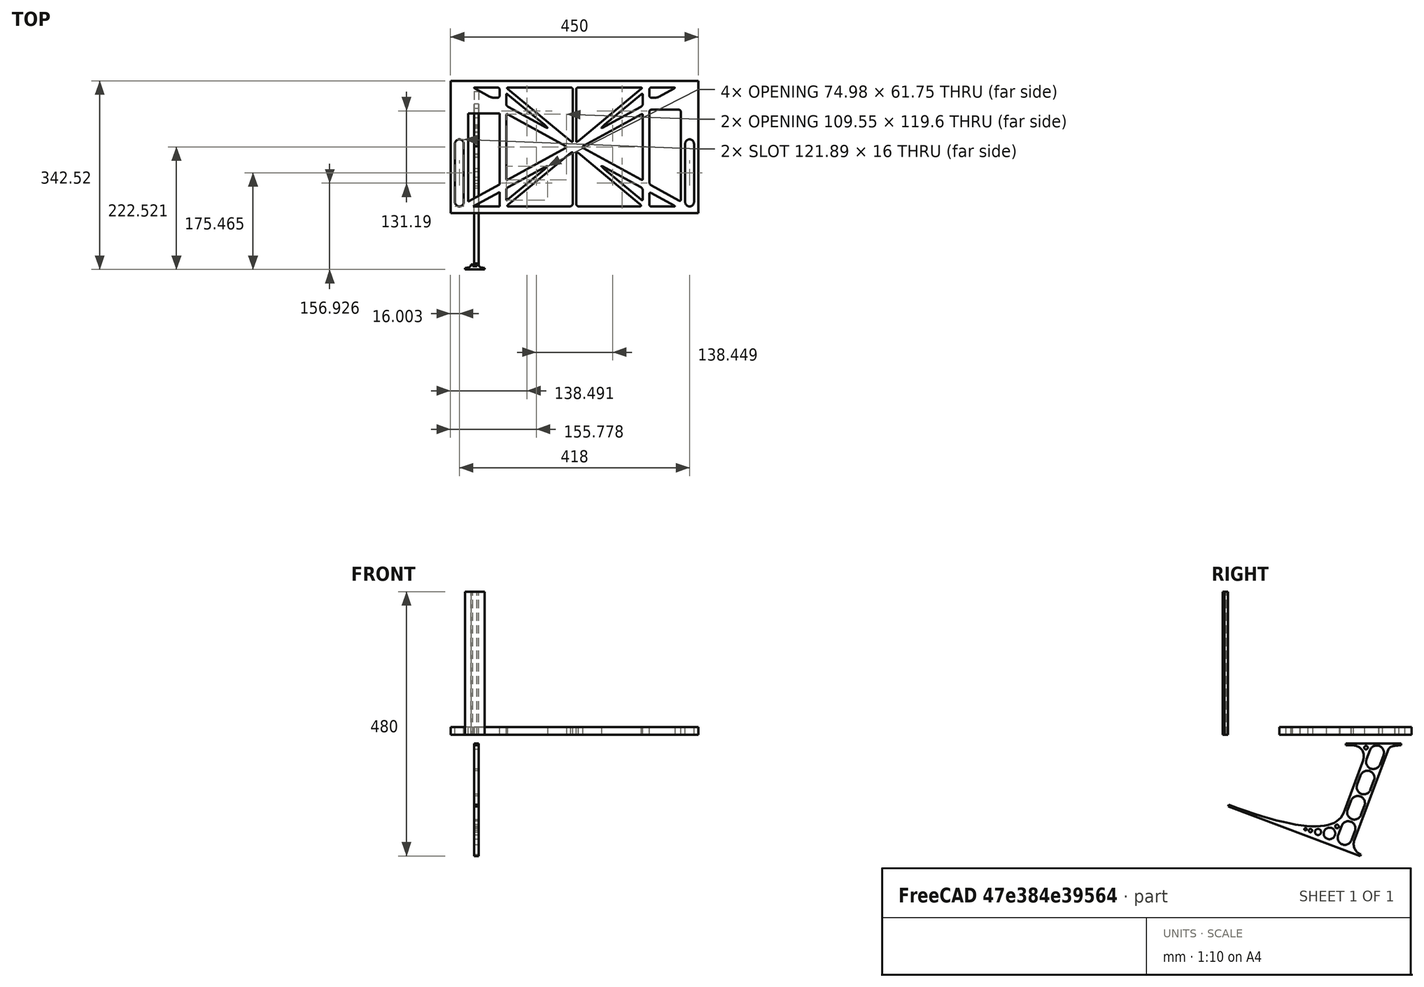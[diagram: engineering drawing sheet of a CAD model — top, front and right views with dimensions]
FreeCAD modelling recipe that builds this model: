
FCSTD DOCUMENT  (FreeCAD 0.19R0.19.2)
Label: laptopStand123FCStd
License: All rights reserved
LicenseURL: http://en.wikipedia.org/wiki/All_rights_reserved
objects: Sketcher::SketchObject×3, Part::Extrusion×3
note: 6 computed .brp shape members not serialized (recipe doc carries the construction recipe); baked Part::Feature solids carry a one-line shape summary decoded from their .brp

FEATURE [Sketcher::SketchObject] Sketch
  FullyConstrained = false
  sketch-geometry (356):
    g0: LineSegment StartX=-10.9272 StartY=-82.7794 StartZ=0 EndX=46.0728 EndY=-51.4823 EndZ=0
    g1: LineSegment StartX=-10.9272 StartY=77.3346 StartZ=0 EndX=-10.9272 EndY=-82.7794 EndZ=0
    g2: LineSegment StartX=46.0728 StartY=-65.424 StartZ=0 EndX=-1.92719 EndY=-91.7794 EndZ=0
    g3: LineSegment StartX=46.0728 StartY=-65.424 StartZ=0 EndX=46.0728 EndY=-91.7794 EndZ=0
    g4: LineSegment StartX=46.0728 StartY=77.3346 StartZ=0 EndX=46.0728 EndY=-51.4823 EndZ=0
    g5: LineSegment StartX=-42.9272 StartY=136.221 StartZ=0 EndX=-42.9272 EndY=-103.779 EndZ=0
    g6: LineSegment StartX=407.073 StartY=136.221 StartZ=0 EndX=407.073 EndY=-103.779 EndZ=0
    g7: ArcOfCircle CenterX=-26.9272 CenterY=22.1087 CenterZ=0 NormalX=0 NormalY=0 NormalZ=1 AngleXU=0 Radius=8 StartAngle=1e-16 EndAngle=3.14159
    g8: ArcOfCircle CenterX=-26.9272 CenterY=-83.7794 CenterZ=0 NormalX=0 NormalY=0 NormalZ=1 AngleXU=0 Radius=8 StartAngle=3.14159 EndAngle=6.28319
    g9: LineSegment StartX=-34.9272 StartY=22.1087 StartZ=0 EndX=-34.9272 EndY=-83.7794 EndZ=0
    g10: LineSegment StartX=-18.9272 StartY=22.1087 StartZ=0 EndX=-18.9272 EndY=-83.7794 EndZ=0
    g11: ArcOfCircle CenterX=391.073 CenterY=22.1087 CenterZ=0 NormalX=0 NormalY=0 NormalZ=1 AngleXU=0 Radius=8 StartAngle=-4.4e-15 EndAngle=3.14159
    g12: LineSegment StartX=399.073 StartY=22.1087 StartZ=0 EndX=399.073 EndY=-83.7794 EndZ=0
    g13: LineSegment StartX=383.073 StartY=22.1087 StartZ=0 EndX=383.073 EndY=-83.7794 EndZ=0
    g14: ArcOfCircle CenterX=391.073 CenterY=-83.7794 CenterZ=0 NormalX=0 NormalY=0 NormalZ=1 AngleXU=0 Radius=8 StartAngle=3.14159 EndAngle=6.28319
    g15: Circle CenterX=175.022 CenterY=27.0628 CenterZ=0 NormalX=0 NormalY=0 NormalZ=1 AngleXU=0 Radius=1
    g16: Circle CenterX=179.022 CenterY=24.8665 CenterZ=0 NormalX=0 NormalY=0 NormalZ=1 AngleXU=0 Radius=1
    g17: Circle CenterX=179.022 CenterY=27.0628 CenterZ=0 NormalX=0 NormalY=0 NormalZ=1 AngleXU=0 Radius=1
    g18: BSplineCurve PolesCount=3 KnotsCount=2 Degree=2 IsPeriodic=0
    g19: GeomPoint X=175.022 Y=27.0628 Z=0
    g20: GeomPoint X=179.022 Y=27.0628 Z=0
    g21: Circle CenterX=189.124 CenterY=27.0628 CenterZ=0 NormalX=0 NormalY=0 NormalZ=1 AngleXU=0 Radius=1
    g22: Circle CenterX=185.124 CenterY=24.8665 CenterZ=0 NormalX=0 NormalY=0 NormalZ=1 AngleXU=0 Radius=1
    g23: Circle CenterX=185.124 CenterY=27.0628 CenterZ=0 NormalX=0 NormalY=0 NormalZ=1 AngleXU=0 Radius=1
    g24: BSplineCurve PolesCount=3 KnotsCount=2 Degree=2 IsPeriodic=0
    g25: GeomPoint X=189.124 Y=27.0628 Z=0
    g26: GeomPoint X=185.124 Y=27.0628 Z=0
    g27: Circle CenterX=175.022 CenterY=5.37834 CenterZ=0 NormalX=0 NormalY=0 NormalZ=1 AngleXU=0 Radius=1
    g28: Circle CenterX=179.022 CenterY=7.57463 CenterZ=0 NormalX=0 NormalY=0 NormalZ=1 AngleXU=0 Radius=1
    g29: Circle CenterX=179.022 CenterY=5.34704 CenterZ=0 NormalX=0 NormalY=0 NormalZ=1 AngleXU=0 Radius=1
    g30: BSplineCurve PolesCount=3 KnotsCount=2 Degree=2 IsPeriodic=0
    g31: GeomPoint X=175.022 Y=5.37834 Z=0
    g32: GeomPoint X=179.022 Y=5.34704 Z=0
    g33: Circle CenterX=189.124 CenterY=5.37834 CenterZ=0 NormalX=0 NormalY=0 NormalZ=1 AngleXU=0 Radius=1
    g34: Circle CenterX=185.124 CenterY=7.57463 CenterZ=0 NormalX=0 NormalY=0 NormalZ=1 AngleXU=0 Radius=1
    g35: Circle CenterX=185.124 CenterY=5.34704 CenterZ=0 NormalX=0 NormalY=0 NormalZ=1 AngleXU=0 Radius=1
    g36: BSplineCurve PolesCount=3 KnotsCount=2 Degree=2 IsPeriodic=0
    g37: GeomPoint X=189.124 Y=5.37834 Z=0
    g38: GeomPoint X=185.124 Y=5.34704 Z=0
    g39: Circle CenterX=165.871 CenterY=18.1458 CenterZ=0 NormalX=0 NormalY=0 NormalZ=1 AngleXU=0 Radius=1
    g40: Circle CenterX=169.377 CenterY=16.2206 CenterZ=0 NormalX=0 NormalY=0 NormalZ=1 AngleXU=0 Radius=1
    g41: Circle CenterX=165.871 CenterY=14.2954 CenterZ=0 NormalX=0 NormalY=0 NormalZ=1 AngleXU=0 Radius=1
    g42: BSplineCurve PolesCount=3 KnotsCount=2 Degree=2 IsPeriodic=0
    g43: GeomPoint X=165.871 Y=18.1458 Z=0
    g44: GeomPoint X=165.871 Y=14.2954 Z=0
    g45: Circle CenterX=198.275 CenterY=18.1458 CenterZ=0 NormalX=0 NormalY=0 NormalZ=1 AngleXU=0 Radius=1
    g46: Circle CenterX=194.768 CenterY=16.2206 CenterZ=0 NormalX=0 NormalY=0 NormalZ=1 AngleXU=0 Radius=1
    g47: Circle CenterX=198.275 CenterY=14.2954 CenterZ=0 NormalX=0 NormalY=0 NormalZ=1 AngleXU=0 Radius=1
    g48: BSplineCurve PolesCount=3 KnotsCount=2 Degree=2 IsPeriodic=0
    g49: GeomPoint X=198.275 Y=18.1458 Z=0
    g50: GeomPoint X=198.275 Y=14.2954 Z=0
    g51: LineSegment StartX=407.073 StartY=-103.779 StartZ=0 EndX=-42.9272 EndY=-103.779 EndZ=0
    g52: LineSegment StartX=407.073 StartY=136.221 StartZ=0 EndX=-42.9272 EndY=136.221 EndZ=0
    g53: LineSegment StartX=46.0728 StartY=77.3346 StartZ=0 EndX=-10.9272 EndY=77.3346 EndZ=0
    g54: Circle CenterX=125.607 CenterY=54.1951 CenterZ=0 NormalX=0 NormalY=0 NormalZ=1 AngleXU=0 Radius=1
    g55: Circle CenterX=139.632 CenterY=46.4944 CenterZ=0 NormalX=0 NormalY=0 NormalZ=1 AngleXU=0 Radius=1
    g56: Circle CenterX=127.326 CenterY=56.7187 CenterZ=0 NormalX=0 NormalY=0 NormalZ=1 AngleXU=0 Radius=1
    g57: BSplineCurve PolesCount=3 KnotsCount=2 Degree=2 IsPeriodic=0
    g58: GeomPoint X=125.607 Y=54.1951 Z=0
    g59: GeomPoint X=127.326 Y=56.7187 Z=0
    g60: Circle CenterX=236.821 CenterY=56.7187 CenterZ=0 NormalX=0 NormalY=0 NormalZ=1 AngleXU=0 Radius=1
    g61: Circle CenterX=224.513 CenterY=46.4944 CenterZ=0 NormalX=0 NormalY=0 NormalZ=1 AngleXU=0 Radius=1
    g62: Circle CenterX=238.538 CenterY=54.1951 CenterZ=0 NormalX=0 NormalY=0 NormalZ=1 AngleXU=0 Radius=1
    g63: BSplineCurve PolesCount=3 KnotsCount=2 Degree=2 IsPeriodic=0
    g64: GeomPoint X=236.821 Y=56.7187 Z=0
    g65: GeomPoint X=238.538 Y=54.1951 Z=0
    g66: Circle CenterX=238.538 CenterY=-21.7539 CenterZ=0 NormalX=0 NormalY=0 NormalZ=1 AngleXU=0 Radius=1
    g67: Circle CenterX=224.513 CenterY=-14.0532 CenterZ=0 NormalX=0 NormalY=0 NormalZ=1 AngleXU=0 Radius=1
    g68: Circle CenterX=236.821 CenterY=-24.2775 CenterZ=0 NormalX=0 NormalY=0 NormalZ=1 AngleXU=0 Radius=1
    g69: BSplineCurve PolesCount=3 KnotsCount=2 Degree=2 IsPeriodic=0
    g70: GeomPoint X=238.538 Y=-21.7539 Z=0
    g71: GeomPoint X=236.821 Y=-24.2775 Z=0
    g72: Circle CenterX=125.607 CenterY=-21.7539 CenterZ=0 NormalX=0 NormalY=0 NormalZ=1 AngleXU=0 Radius=1
    g73: Circle CenterX=139.632 CenterY=-14.0532 CenterZ=0 NormalX=0 NormalY=0 NormalZ=1 AngleXU=0 Radius=1
    g74: Circle CenterX=127.325 CenterY=-24.2775 CenterZ=0 NormalX=0 NormalY=0 NormalZ=1 AngleXU=0 Radius=1
    g75: BSplineCurve PolesCount=3 KnotsCount=2 Degree=2 IsPeriodic=0
    g76: GeomPoint X=125.607 Y=-21.7539 Z=0
    g77: GeomPoint X=127.325 Y=-24.2775 Z=0
    g78: Circle CenterX=302.996 CenterY=111.695 CenterZ=0 NormalX=0 NormalY=0 NormalZ=1 AngleXU=0 Radius=1
    g79: Circle CenterX=306.073 CenterY=114.251 CenterZ=0 NormalX=0 NormalY=0 NormalZ=1 AngleXU=0 Radius=1
    g80: Circle CenterX=306.073 CenterY=110.251 CenterZ=0 NormalX=0 NormalY=0 NormalZ=1 AngleXU=0 Radius=1
    g81: BSplineCurve PolesCount=3 KnotsCount=2 Degree=2 IsPeriodic=0
    g82: GeomPoint X=302.996 Y=111.695 Z=0
    g83: GeomPoint X=306.073 Y=110.251 Z=0
    g84: Circle CenterX=306.073 CenterY=95.2763 CenterZ=0 NormalX=0 NormalY=0 NormalZ=1 AngleXU=0 Radius=1
    g85: Circle CenterX=306.073 CenterY=91.2763 CenterZ=0 NormalX=0 NormalY=0 NormalZ=1 AngleXU=0 Radius=1
    g86: Circle CenterX=302.567 CenterY=89.3511 CenterZ=0 NormalX=0 NormalY=0 NormalZ=1 AngleXU=0 Radius=1
    g87: BSplineCurve PolesCount=3 KnotsCount=2 Degree=2 IsPeriodic=0
    g88: GeomPoint X=306.073 Y=95.2763 Z=0
    g89: GeomPoint X=302.567 Y=89.3511 Z=0
    g90: LineSegment StartX=306.073 StartY=110.251 StartZ=0 EndX=306.073 EndY=95.2763 EndZ=0
    g91: LineSegment StartX=302.996 StartY=111.695 StartZ=0 EndX=236.821 EndY=56.7187 EndZ=0
    g92: LineSegment StartX=238.538 StartY=54.1951 StartZ=0 EndX=302.567 EndY=89.3511 EndZ=0
    g93: Circle CenterX=61.1496 CenterY=111.695 CenterZ=0 NormalX=0 NormalY=0 NormalZ=1 AngleXU=0 Radius=1
    g94: Circle CenterX=58.0728 CenterY=114.251 CenterZ=0 NormalX=0 NormalY=0 NormalZ=1 AngleXU=0 Radius=1
    g95: Circle CenterX=58.0728 CenterY=110.251 CenterZ=0 NormalX=0 NormalY=0 NormalZ=1 AngleXU=0 Radius=1
    g96: BSplineCurve PolesCount=3 KnotsCount=2 Degree=2 IsPeriodic=0
    g97: GeomPoint X=61.1496 Y=111.695 Z=0
    g98: GeomPoint X=58.0728 Y=110.251 Z=0
    g99: Circle CenterX=61.5791 CenterY=89.3511 CenterZ=0 NormalX=0 NormalY=0 NormalZ=1 AngleXU=0 Radius=1
    g100: Circle CenterX=58.0728 CenterY=91.2763 CenterZ=0 NormalX=0 NormalY=0 NormalZ=1 AngleXU=0 Radius=1
    g101: Circle CenterX=58.0728 CenterY=95.2763 CenterZ=0 NormalX=0 NormalY=0 NormalZ=1 AngleXU=0 Radius=1
    g102: BSplineCurve PolesCount=3 KnotsCount=2 Degree=2 IsPeriodic=0
    g103: GeomPoint X=61.5791 Y=89.3511 Z=0
    g104: GeomPoint X=58.0728 Y=95.2763 Z=0
    g105: LineSegment StartX=58.0728 StartY=110.251 StartZ=0 EndX=58.0728 EndY=95.2763 EndZ=0
    g106: LineSegment StartX=61.1496 StartY=111.695 StartZ=0 EndX=127.326 EndY=56.7187 EndZ=0
    g107: LineSegment StartX=125.607 StartY=54.1951 StartZ=0 EndX=61.5791 EndY=89.3511 EndZ=0
    g108: Circle CenterX=61.5791 CenterY=-56.9099 CenterZ=0 NormalX=0 NormalY=0 NormalZ=1 AngleXU=0 Radius=1
    g109: Circle CenterX=58.0728 CenterY=-58.8351 CenterZ=0 NormalX=0 NormalY=0 NormalZ=1 AngleXU=0 Radius=1
    g110: Circle CenterX=58.0728 CenterY=-62.8351 CenterZ=0 NormalX=0 NormalY=0 NormalZ=1 AngleXU=0 Radius=1
    g111: BSplineCurve PolesCount=3 KnotsCount=2 Degree=2 IsPeriodic=0
    g112: GeomPoint X=61.5791 Y=-56.9099 Z=0
    g113: GeomPoint X=58.0728 Y=-62.8351 Z=0
    g114: Circle CenterX=58.0728 CenterY=-77.8102 CenterZ=0 NormalX=0 NormalY=0 NormalZ=1 AngleXU=0 Radius=1
    g115: Circle CenterX=58.0728 CenterY=-81.8102 CenterZ=0 NormalX=0 NormalY=0 NormalZ=1 AngleXU=0 Radius=1
    g116: Circle CenterX=61.1496 CenterY=-79.2541 CenterZ=0 NormalX=0 NormalY=0 NormalZ=1 AngleXU=0 Radius=1
    g117: BSplineCurve PolesCount=3 KnotsCount=2 Degree=2 IsPeriodic=0
    g118: GeomPoint X=58.0728 Y=-77.8102 Z=0
    g119: GeomPoint X=61.1496 Y=-79.2541 Z=0
    g120: LineSegment StartX=58.0728 StartY=-62.8351 StartZ=0 EndX=58.0728 EndY=-77.8102 EndZ=0
    g121: LineSegment StartX=61.1496 StartY=-79.2541 StartZ=0 EndX=127.325 EndY=-24.2775 EndZ=0
    g122: LineSegment StartX=125.607 StartY=-21.7539 StartZ=0 EndX=61.5791 EndY=-56.9099 EndZ=0
    g123: Circle CenterX=302.567 CenterY=-56.9099 CenterZ=0 NormalX=0 NormalY=0 NormalZ=1 AngleXU=0 Radius=1
    g124: Circle CenterX=306.073 CenterY=-58.8351 CenterZ=0 NormalX=0 NormalY=0 NormalZ=1 AngleXU=0 Radius=1
    g125: Circle CenterX=306.073 CenterY=-62.8351 CenterZ=0 NormalX=0 NormalY=0 NormalZ=1 AngleXU=0 Radius=1
    g126: BSplineCurve PolesCount=3 KnotsCount=2 Degree=2 IsPeriodic=0
    g127: GeomPoint X=302.567 Y=-56.9099 Z=0
    g128: GeomPoint X=306.073 Y=-62.8351 Z=0
    g129: Circle CenterX=302.996 CenterY=-79.2541 CenterZ=0 NormalX=0 NormalY=0 NormalZ=1 AngleXU=0 Radius=1
    g130: Circle CenterX=306.073 CenterY=-81.8102 CenterZ=0 NormalX=0 NormalY=0 NormalZ=1 AngleXU=0 Radius=1
    g131: Circle CenterX=306.073 CenterY=-77.8102 CenterZ=0 NormalX=0 NormalY=0 NormalZ=1 AngleXU=0 Radius=1
    g132: BSplineCurve PolesCount=3 KnotsCount=2 Degree=2 IsPeriodic=0
    g133: GeomPoint X=302.996 Y=-79.2541 Z=0
    g134: GeomPoint X=306.073 Y=-77.8102 Z=0
    g135: LineSegment StartX=306.073 StartY=-62.8351 StartZ=0 EndX=306.073 EndY=-77.8102 EndZ=0
    g136: LineSegment StartX=302.996 StartY=-79.2541 StartZ=0 EndX=236.821 EndY=-24.2775 EndZ=0
    g137: LineSegment StartX=238.538 StartY=-21.7539 StartZ=0 EndX=302.567 EndY=-56.9099 EndZ=0
    g138: Circle CenterX=61.6457 CenterY=-88.8112 CenterZ=0 NormalX=0 NormalY=0 NormalZ=1 AngleXU=0 Radius=1
    g139: Circle CenterX=58.0728 CenterY=-91.7794 CenterZ=0 NormalX=0 NormalY=0 NormalZ=1 AngleXU=0 Radius=1
    g140: Circle CenterX=63.9135 CenterY=-91.7794 CenterZ=0 NormalX=0 NormalY=0 NormalZ=1 AngleXU=0 Radius=1
    g141: BSplineCurve PolesCount=3 KnotsCount=2 Degree=2 IsPeriodic=0
    g142: GeomPoint X=61.6457 Y=-88.8112 Z=0
    g143: GeomPoint X=63.9135 Y=-91.7794 Z=0
    g144: Circle CenterX=179.022 CenterY=-85.8163 CenterZ=0 NormalX=0 NormalY=0 NormalZ=1 AngleXU=0 Radius=1
    g145: Circle CenterX=179.022 CenterY=-91.7794 CenterZ=0 NormalX=0 NormalY=0 NormalZ=1 AngleXU=0 Radius=1
    g146: Circle CenterX=171.895 CenterY=-91.7794 CenterZ=0 NormalX=0 NormalY=0 NormalZ=1 AngleXU=0 Radius=1
    g147: BSplineCurve PolesCount=3 KnotsCount=2 Degree=2 IsPeriodic=0
    g148: GeomPoint X=179.022 Y=-85.8163 Z=0
    g149: GeomPoint X=171.895 Y=-91.7794 Z=0
    g150: Circle CenterX=185.124 CenterY=-86.2028 CenterZ=0 NormalX=0 NormalY=0 NormalZ=1 AngleXU=0 Radius=1
    g151: Circle CenterX=185.124 CenterY=-91.7794 CenterZ=0 NormalX=0 NormalY=0 NormalZ=1 AngleXU=0 Radius=1
    g152: Circle CenterX=191.747 CenterY=-91.7794 CenterZ=0 NormalX=0 NormalY=0 NormalZ=1 AngleXU=0 Radius=1
    g153: BSplineCurve PolesCount=3 KnotsCount=2 Degree=2 IsPeriodic=0
    g154: GeomPoint X=185.124 Y=-86.2028 Z=0
    g155: GeomPoint X=191.747 Y=-91.7794 Z=0
    g156: Circle CenterX=299.888 CenterY=-86.6413 CenterZ=0 NormalX=0 NormalY=0 NormalZ=1 AngleXU=0 Radius=1
    g157: Circle CenterX=306.073 CenterY=-91.7794 CenterZ=0 NormalX=0 NormalY=0 NormalZ=1 AngleXU=0 Radius=1
    g158: Circle CenterX=298.776 CenterY=-91.7794 CenterZ=0 NormalX=0 NormalY=0 NormalZ=1 AngleXU=0 Radius=1
    g159: BSplineCurve PolesCount=3 KnotsCount=2 Degree=2 IsPeriodic=0
    g160: GeomPoint X=299.888 Y=-86.6413 Z=0
    g161: GeomPoint X=298.776 Y=-91.7794 Z=0
    g162: LineSegment StartX=189.124 StartY=5.37834 StartZ=0 EndX=299.888 EndY=-86.6413 EndZ=0
    g163: LineSegment StartX=298.776 StartY=-91.7794 StartZ=0 EndX=191.747 EndY=-91.7794 EndZ=0
    g164: LineSegment StartX=185.124 StartY=-86.2028 StartZ=0 EndX=185.124 EndY=5.34704 EndZ=0
    g165: LineSegment StartX=179.022 StartY=5.34704 StartZ=0 EndX=179.022 EndY=-85.8163 EndZ=0
    g166: LineSegment StartX=171.895 StartY=-91.7794 StartZ=0 EndX=63.9135 EndY=-91.7794 EndZ=0
    g167: LineSegment StartX=61.6457 StartY=-88.8112 StartZ=0 EndX=175.022 EndY=5.37834 EndZ=0
    g168: Circle CenterX=302.073 CenterY=124.221 CenterZ=0 NormalX=0 NormalY=0 NormalZ=1 AngleXU=0 Radius=1
    g169: Circle CenterX=306.073 CenterY=124.221 CenterZ=0 NormalX=0 NormalY=0 NormalZ=1 AngleXU=0 Radius=1
    g170: Circle CenterX=302.996 CenterY=121.665 CenterZ=0 NormalX=0 NormalY=0 NormalZ=1 AngleXU=0 Radius=1
    g171: BSplineCurve PolesCount=3 KnotsCount=2 Degree=2 IsPeriodic=0
    g172: GeomPoint X=302.073 Y=124.221 Z=0
    g173: GeomPoint X=302.996 Y=121.665 Z=0
    g174: Circle CenterX=189.124 CenterY=124.221 CenterZ=0 NormalX=0 NormalY=0 NormalZ=1 AngleXU=0 Radius=1
    g175: Circle CenterX=185.124 CenterY=124.221 CenterZ=0 NormalX=0 NormalY=0 NormalZ=1 AngleXU=0 Radius=1
    g176: Circle CenterX=185.124 CenterY=120.221 CenterZ=0 NormalX=0 NormalY=0 NormalZ=1 AngleXU=0 Radius=1
    g177: BSplineCurve PolesCount=3 KnotsCount=2 Degree=2 IsPeriodic=0
    g178: GeomPoint X=189.124 Y=124.221 Z=0
    g179: GeomPoint X=185.124 Y=120.221 Z=0
    g180: Circle CenterX=175.022 CenterY=124.221 CenterZ=0 NormalX=0 NormalY=0 NormalZ=1 AngleXU=0 Radius=1
    g181: Circle CenterX=179.022 CenterY=124.221 CenterZ=0 NormalX=0 NormalY=0 NormalZ=1 AngleXU=0 Radius=1
    g182: Circle CenterX=179.022 CenterY=120.221 CenterZ=0 NormalX=0 NormalY=0 NormalZ=1 AngleXU=0 Radius=1
    g183: BSplineCurve PolesCount=3 KnotsCount=2 Degree=2 IsPeriodic=0
    g184: GeomPoint X=175.022 Y=124.221 Z=0
    g185: GeomPoint X=179.022 Y=120.221 Z=0
    g186: Circle CenterX=62.0728 CenterY=124.221 CenterZ=0 NormalX=0 NormalY=0 NormalZ=1 AngleXU=0 Radius=1
    g187: Circle CenterX=58.0728 CenterY=124.221 CenterZ=0 NormalX=0 NormalY=0 NormalZ=1 AngleXU=0 Radius=1
    g188: Circle CenterX=61.1496 CenterY=121.665 CenterZ=0 NormalX=0 NormalY=0 NormalZ=1 AngleXU=0 Radius=1
    g189: BSplineCurve PolesCount=3 KnotsCount=2 Degree=2 IsPeriodic=0
    g190: GeomPoint X=62.0728 Y=124.221 Z=0
    g191: GeomPoint X=61.1496 Y=121.665 Z=0
    g192: LineSegment StartX=62.0728 StartY=124.221 StartZ=0 EndX=175.022 EndY=124.221 EndZ=0
    g193: LineSegment StartX=179.022 StartY=120.221 StartZ=0 EndX=179.022 EndY=27.0628 EndZ=0
    g194: LineSegment StartX=185.124 StartY=27.0628 StartZ=0 EndX=185.124 EndY=120.221 EndZ=0
    g195: LineSegment StartX=189.124 StartY=124.221 StartZ=0 EndX=302.073 EndY=124.221 EndZ=0
    g196: LineSegment StartX=302.996 StartY=121.665 StartZ=0 EndX=189.124 EndY=27.0628 EndZ=0
    g197: LineSegment StartX=175.022 StartY=27.0628 StartZ=0 EndX=61.1496 EndY=121.665 EndZ=0
    g198: Circle CenterX=61.5791 CenterY=75.4095 CenterZ=0 NormalX=0 NormalY=0 NormalZ=1 AngleXU=0 Radius=1
    g199: Circle CenterX=58.0728 CenterY=77.3346 CenterZ=0 NormalX=0 NormalY=0 NormalZ=1 AngleXU=0 Radius=1
    g200: Circle CenterX=58.0728 CenterY=73.3346 CenterZ=0 NormalX=0 NormalY=0 NormalZ=1 AngleXU=0 Radius=1
    g201: BSplineCurve PolesCount=3 KnotsCount=2 Degree=2 IsPeriodic=0
    g202: GeomPoint X=61.5791 Y=75.4095 Z=0
    g203: GeomPoint X=58.0728 Y=73.3346 Z=0
    g204: Circle CenterX=58.0728 CenterY=-40.8935 CenterZ=0 NormalX=0 NormalY=0 NormalZ=1 AngleXU=0 Radius=1
    g205: Circle CenterX=58.0728 CenterY=-44.8935 CenterZ=0 NormalX=0 NormalY=0 NormalZ=1 AngleXU=0 Radius=1
    g206: Circle CenterX=61.5791 CenterY=-42.9683 CenterZ=0 NormalX=0 NormalY=0 NormalZ=1 AngleXU=0 Radius=1
    g207: BSplineCurve PolesCount=3 KnotsCount=2 Degree=2 IsPeriodic=0
    g208: GeomPoint X=58.0728 Y=-40.8935 Z=0
    g209: GeomPoint X=61.5791 Y=-42.9683 Z=0
    g210: LineSegment StartX=61.5791 StartY=-42.9683 StartZ=0 EndX=165.871 EndY=14.2954 EndZ=0
    g211: LineSegment StartX=165.871 StartY=18.1458 StartZ=0 EndX=61.5791 EndY=75.4095 EndZ=0
    g212: LineSegment StartX=58.0728 StartY=73.3346 StartZ=0 EndX=58.0728 EndY=-40.8935 EndZ=0
    g213: Circle CenterX=302.567 CenterY=-42.9683 CenterZ=0 NormalX=0 NormalY=0 NormalZ=1 AngleXU=0 Radius=1
    g214: Circle CenterX=306.073 CenterY=-44.8935 CenterZ=0 NormalX=0 NormalY=0 NormalZ=1 AngleXU=0 Radius=1
    g215: Circle CenterX=306.073 CenterY=-40.8935 CenterZ=0 NormalX=0 NormalY=0 NormalZ=1 AngleXU=0 Radius=1
    g216: BSplineCurve PolesCount=3 KnotsCount=2 Degree=2 IsPeriodic=0
    g217: GeomPoint X=302.567 Y=-42.9683 Z=0
    g218: GeomPoint X=306.073 Y=-40.8935 Z=0
    g219: Circle CenterX=306.073 CenterY=73.3346 CenterZ=0 NormalX=0 NormalY=0 NormalZ=1 AngleXU=0 Radius=1
    g220: Circle CenterX=306.073 CenterY=77.3346 CenterZ=0 NormalX=0 NormalY=0 NormalZ=1 AngleXU=0 Radius=1
    g221: Circle CenterX=302.567 CenterY=75.4095 CenterZ=0 NormalX=0 NormalY=0 NormalZ=1 AngleXU=0 Radius=1
    g222: BSplineCurve PolesCount=3 KnotsCount=2 Degree=2 IsPeriodic=0
    g223: GeomPoint X=306.073 Y=73.3346 Z=0
    g224: GeomPoint X=302.567 Y=75.4095 Z=0
    g225: LineSegment StartX=302.567 StartY=-42.9683 StartZ=0 EndX=198.275 EndY=14.2954 EndZ=0
    g226: LineSegment StartX=198.275 StartY=18.1458 StartZ=0 EndX=302.567 EndY=75.4095 EndZ=0
    g227: LineSegment StartX=306.073 StartY=73.3346 StartZ=0 EndX=306.073 EndY=-40.8935 EndZ=0
    g228: LineSegment StartX=322.073 StartY=105.865 StartZ=0 EndX=328.643 EndY=105.865 EndZ=0
    g229: LineSegment StartX=318.073 StartY=120.221 StartZ=0 EndX=318.073 EndY=109.865 EndZ=0
    g230: LineSegment StartX=336.157 StartY=107.779 StartZ=0 EndX=362.567 EndY=122.294 EndZ=0
    g231: Circle CenterX=362.073 CenterY=124.221 CenterZ=0 NormalX=0 NormalY=0 NormalZ=1 AngleXU=0 Radius=1
    g232: Circle CenterX=366.073 CenterY=124.221 CenterZ=0 NormalX=0 NormalY=0 NormalZ=1 AngleXU=0 Radius=1
    g233: Circle CenterX=362.567 CenterY=122.294 CenterZ=0 NormalX=0 NormalY=0 NormalZ=1 AngleXU=0 Radius=1
    g234: BSplineCurve PolesCount=3 KnotsCount=2 Degree=2 IsPeriodic=0
    g235: GeomPoint X=362.073 Y=124.221 Z=0
    g236: GeomPoint X=362.567 Y=122.294 Z=0
    g237: Circle CenterX=322.073 CenterY=124.221 CenterZ=0 NormalX=0 NormalY=0 NormalZ=1 AngleXU=0 Radius=1
    g238: Circle CenterX=318.073 CenterY=124.221 CenterZ=0 NormalX=0 NormalY=0 NormalZ=1 AngleXU=0 Radius=1
    g239: Circle CenterX=318.073 CenterY=120.221 CenterZ=0 NormalX=0 NormalY=0 NormalZ=1 AngleXU=0 Radius=1
    g240: BSplineCurve PolesCount=3 KnotsCount=2 Degree=2 IsPeriodic=0
    g241: GeomPoint X=322.073 Y=124.221 Z=0
    g242: GeomPoint X=318.073 Y=120.221 Z=0
    g243: Circle CenterX=322.073 CenterY=105.865 CenterZ=0 NormalX=0 NormalY=0 NormalZ=1 AngleXU=0 Radius=1
    g244: Circle CenterX=318.073 CenterY=105.865 CenterZ=0 NormalX=0 NormalY=0 NormalZ=1 AngleXU=0 Radius=1
    g245: Circle CenterX=318.073 CenterY=109.865 CenterZ=0 NormalX=0 NormalY=0 NormalZ=1 AngleXU=0 Radius=1
    g246: BSplineCurve PolesCount=3 KnotsCount=2 Degree=2 IsPeriodic=0
    g247: GeomPoint X=322.073 Y=105.865 Z=0
    g248: GeomPoint X=318.073 Y=109.865 Z=0
    g249: Circle CenterX=336.157 CenterY=107.779 CenterZ=0 NormalX=0 NormalY=0 NormalZ=1 AngleXU=0 Radius=1
    g250: Circle CenterX=332.651 CenterY=105.853 CenterZ=0 NormalX=0 NormalY=0 NormalZ=1 AngleXU=0 Radius=1
    g251: Circle CenterX=328.643 CenterY=105.865 CenterZ=0 NormalX=0 NormalY=0 NormalZ=1 AngleXU=0 Radius=1
    g252: BSplineCurve PolesCount=3 KnotsCount=2 Degree=2 IsPeriodic=0
    g253: GeomPoint X=336.157 Y=107.779 Z=0
    g254: GeomPoint X=328.643 Y=105.865 Z=0
    g255: LineSegment StartX=322.073 StartY=124.221 StartZ=0 EndX=362.073 EndY=124.221 EndZ=0
    g256: Circle CenterX=371.567 CenterY=-80.8644 CenterZ=0 NormalX=0 NormalY=0 NormalZ=1 AngleXU=0 Radius=1
    g257: Circle CenterX=375.073 CenterY=-82.7896 CenterZ=0 NormalX=0 NormalY=0 NormalZ=1 AngleXU=0 Radius=1
    g258: Circle CenterX=375.073 CenterY=-78.7896 CenterZ=0 NormalX=0 NormalY=0 NormalZ=1 AngleXU=0 Radius=1
    g259: BSplineCurve PolesCount=3 KnotsCount=2 Degree=2 IsPeriodic=0
    g260: GeomPoint X=371.567 Y=-80.8644 Z=0
    g261: GeomPoint X=375.073 Y=-78.7896 Z=0
    g262: Circle CenterX=321.579 CenterY=-53.4075 CenterZ=0 NormalX=0 NormalY=0 NormalZ=1 AngleXU=0 Radius=1
    g263: Circle CenterX=318.073 CenterY=-51.4823 CenterZ=0 NormalX=0 NormalY=0 NormalZ=1 AngleXU=0 Radius=1
    g264: Circle CenterX=318.073 CenterY=-47.4823 CenterZ=0 NormalX=0 NormalY=0 NormalZ=1 AngleXU=0 Radius=1
    g265: BSplineCurve PolesCount=3 KnotsCount=2 Degree=2 IsPeriodic=0
    g266: GeomPoint X=321.579 Y=-53.4075 Z=0
    g267: GeomPoint X=318.073 Y=-47.4823 Z=0
    g268: Circle CenterX=318.073 CenterY=79.9235 CenterZ=0 NormalX=0 NormalY=0 NormalZ=1 AngleXU=0 Radius=1
    g269: Circle CenterX=318.073 CenterY=83.9235 CenterZ=0 NormalX=0 NormalY=0 NormalZ=1 AngleXU=0 Radius=1
    g270: Circle CenterX=322.073 CenterY=83.9235 CenterZ=0 NormalX=0 NormalY=0 NormalZ=1 AngleXU=0 Radius=1
    g271: BSplineCurve PolesCount=3 KnotsCount=2 Degree=2 IsPeriodic=0
    g272: GeomPoint X=318.073 Y=79.9235 Z=0
    g273: GeomPoint X=322.073 Y=83.9235 Z=0
    g274: Circle CenterX=375.073 CenterY=79.9235 CenterZ=0 NormalX=0 NormalY=0 NormalZ=1 AngleXU=0 Radius=1
    g275: Circle CenterX=375.073 CenterY=83.9235 CenterZ=0 NormalX=0 NormalY=0 NormalZ=1 AngleXU=0 Radius=1
    g276: Circle CenterX=371.073 CenterY=83.9235 CenterZ=0 NormalX=0 NormalY=0 NormalZ=1 AngleXU=0 Radius=1
    g277: BSplineCurve PolesCount=3 KnotsCount=2 Degree=2 IsPeriodic=0
    g278: GeomPoint X=375.073 Y=79.9235 Z=0
    g279: GeomPoint X=371.073 Y=83.9235 Z=0
    g280: LineSegment StartX=322.073 StartY=83.9235 StartZ=0 EndX=371.073 EndY=83.9235 EndZ=0
    g281: LineSegment StartX=375.073 StartY=79.9235 StartZ=0 EndX=375.073 EndY=-78.7896 EndZ=0
    g282: LineSegment StartX=371.567 StartY=-80.8644 StartZ=0 EndX=321.579 EndY=-53.4075 EndZ=0
    g283: LineSegment StartX=318.073 StartY=-47.4823 StartZ=0 EndX=318.073 EndY=79.9235 EndZ=0
    g284: Circle CenterX=321.579 CenterY=-67.3492 CenterZ=0 NormalX=0 NormalY=0 NormalZ=1 AngleXU=0 Radius=1
    g285: Circle CenterX=318.073 CenterY=-65.424 CenterZ=0 NormalX=0 NormalY=0 NormalZ=1 AngleXU=0 Radius=1
    g286: Circle CenterX=318.073 CenterY=-69.424 CenterZ=0 NormalX=0 NormalY=0 NormalZ=1 AngleXU=0 Radius=1
    g287: BSplineCurve PolesCount=3 KnotsCount=2 Degree=2 IsPeriodic=0
    g288: GeomPoint X=321.579 Y=-67.3492 Z=0
    g289: GeomPoint X=318.073 Y=-69.424 Z=0
    g290: Circle CenterX=362.567 CenterY=-89.8542 CenterZ=0 NormalX=0 NormalY=0 NormalZ=1 AngleXU=0 Radius=1
    g291: Circle CenterX=366.073 CenterY=-91.7794 CenterZ=0 NormalX=0 NormalY=0 NormalZ=1 AngleXU=0 Radius=1
    g292: Circle CenterX=362.073 CenterY=-91.7794 CenterZ=0 NormalX=0 NormalY=0 NormalZ=1 AngleXU=0 Radius=1
    g293: BSplineCurve PolesCount=3 KnotsCount=2 Degree=2 IsPeriodic=0
    g294: GeomPoint X=362.567 Y=-89.8542 Z=0
    g295: GeomPoint X=362.073 Y=-91.7794 Z=0
    g296: Circle CenterX=322.073 CenterY=-91.7794 CenterZ=0 NormalX=0 NormalY=0 NormalZ=1 AngleXU=0 Radius=1
    g297: Circle CenterX=318.073 CenterY=-91.7794 CenterZ=0 NormalX=0 NormalY=0 NormalZ=1 AngleXU=0 Radius=1
    g298: Circle CenterX=318.073 CenterY=-87.7794 CenterZ=0 NormalX=0 NormalY=0 NormalZ=1 AngleXU=0 Radius=1
    g299: BSplineCurve PolesCount=3 KnotsCount=2 Degree=2 IsPeriodic=0
    g300: GeomPoint X=322.073 Y=-91.7794 Z=0
    g301: GeomPoint X=318.073 Y=-87.7794 Z=0
    g302: LineSegment StartX=362.567 StartY=-89.8542 StartZ=0 EndX=321.579 EndY=-67.3492 EndZ=0
    g303: LineSegment StartX=318.073 StartY=-69.424 StartZ=0 EndX=318.073 EndY=-87.7794 EndZ=0
    g304: LineSegment StartX=322.073 StartY=-91.7794 StartZ=0 EndX=362.073 EndY=-91.7794 EndZ=0
    g305: Circle CenterX=2.07281 CenterY=124.221 CenterZ=0 NormalX=0 NormalY=0 NormalZ=1 AngleXU=0 Radius=1
    g306: Circle CenterX=1.57905 CenterY=122.295 CenterZ=0 NormalX=0 NormalY=0 NormalZ=1 AngleXU=0 Radius=1
    g307: BSplineCurve PolesCount=3 KnotsCount=2 Degree=2 IsPeriodic=0
    g308: GeomPoint X=2.07281 Y=124.221 Z=0
    g309: GeomPoint X=1.57905 Y=122.295 Z=0
    g310: Circle CenterX=42.0728 CenterY=124.221 CenterZ=0 NormalX=0 NormalY=0 NormalZ=1 AngleXU=0 Radius=1
    g311: Circle CenterX=46.0728 CenterY=124.221 CenterZ=0 NormalX=0 NormalY=0 NormalZ=1 AngleXU=0 Radius=1
    g312: Circle CenterX=46.0728 CenterY=120.221 CenterZ=0 NormalX=0 NormalY=0 NormalZ=1 AngleXU=0 Radius=1
    g313: BSplineCurve PolesCount=3 KnotsCount=2 Degree=2 IsPeriodic=0
    g314: GeomPoint X=42.0728 Y=124.221 Z=0
    g315: GeomPoint X=46.0728 Y=120.221 Z=0
    g316: Circle CenterX=46.0728 CenterY=109.865 CenterZ=0 NormalX=0 NormalY=0 NormalZ=1 AngleXU=0 Radius=1
    g317: Circle CenterX=46.0728 CenterY=105.865 CenterZ=0 NormalX=0 NormalY=0 NormalZ=1 AngleXU=0 Radius=1
    g318: Circle CenterX=42.0728 CenterY=105.865 CenterZ=0 NormalX=0 NormalY=0 NormalZ=1 AngleXU=0 Radius=1
    g319: BSplineCurve PolesCount=3 KnotsCount=2 Degree=2 IsPeriodic=0
    g320: GeomPoint X=46.0728 Y=109.865 Z=0
    g321: GeomPoint X=42.0728 Y=105.865 Z=0
    g322: Circle CenterX=35.5028 CenterY=105.865 CenterZ=0 NormalX=0 NormalY=0 NormalZ=1 AngleXU=0 Radius=1
    g323: Circle CenterX=31.5028 CenterY=105.865 CenterZ=0 NormalX=0 NormalY=0 NormalZ=1 AngleXU=0 Radius=1
    g324: Circle CenterX=27.9965 CenterY=107.79 CenterZ=0 NormalX=0 NormalY=0 NormalZ=1 AngleXU=0 Radius=1
    g325: BSplineCurve PolesCount=3 KnotsCount=2 Degree=2 IsPeriodic=0
    g326: GeomPoint X=35.5028 Y=105.865 Z=0
    g327: GeomPoint X=27.9965 Y=107.79 Z=0
    g328: LineSegment StartX=2.07281 StartY=124.221 StartZ=0 EndX=42.0728 EndY=124.221 EndZ=0
    g329: LineSegment StartX=46.0728 StartY=120.221 StartZ=0 EndX=46.0728 EndY=109.865 EndZ=0
    g330: LineSegment StartX=42.0728 StartY=105.865 StartZ=0 EndX=35.5028 EndY=105.865 EndZ=0
    g331: LineSegment StartX=27.9965 StartY=107.79 StartZ=0 EndX=1.57905 EndY=122.295 EndZ=0
    g332: LineSegment StartX=46.0728 StartY=-65.424 StartZ=0 EndX=46.0728 EndY=-69.424 EndZ=0
    g333: LineSegment StartX=46.0728 StartY=-91.7794 StartZ=0 EndX=46.0728 EndY=-87.7794 EndZ=0
    g334: LineSegment StartX=46.0728 StartY=-91.7794 StartZ=0 EndX=42.0728 EndY=-91.7794 EndZ=0
    g335: LineSegment StartX=-1.92719 StartY=-91.7794 StartZ=0 EndX=2.07281 EndY=-91.7794 EndZ=0
    g336: LineSegment StartX=-1.92719 StartY=-91.7794 StartZ=0 EndX=1.57905 EndY=-89.8542 EndZ=0
    g337: LineSegment StartX=46.0728 StartY=-65.424 StartZ=0 EndX=42.5666 EndY=-67.3492 EndZ=0
    g338: Circle CenterX=42.5666 CenterY=-67.3492 CenterZ=0 NormalX=0 NormalY=0 NormalZ=1 AngleXU=0 Radius=1
    g339: Circle CenterX=46.0728 CenterY=-65.424 CenterZ=0 NormalX=0 NormalY=0 NormalZ=1 AngleXU=0 Radius=1
    g340: Circle CenterX=46.0728 CenterY=-69.424 CenterZ=0 NormalX=0 NormalY=0 NormalZ=1 AngleXU=0 Radius=1
    g341: BSplineCurve PolesCount=3 KnotsCount=2 Degree=2 IsPeriodic=0
    g342: GeomPoint X=42.5666 Y=-67.3492 Z=0
    g343: GeomPoint X=46.0728 Y=-69.424 Z=0
    g344: Circle CenterX=46.0728 CenterY=-87.7794 CenterZ=0 NormalX=0 NormalY=0 NormalZ=1 AngleXU=0 Radius=1
    g345: Circle CenterX=46.0728 CenterY=-91.7794 CenterZ=0 NormalX=0 NormalY=0 NormalZ=1 AngleXU=0 Radius=1
    g346: Circle CenterX=42.0728 CenterY=-91.7794 CenterZ=0 NormalX=0 NormalY=0 NormalZ=1 AngleXU=0 Radius=1
    g347: BSplineCurve PolesCount=3 KnotsCount=2 Degree=2 IsPeriodic=0
    g348: GeomPoint X=46.0728 Y=-87.7794 Z=0
    g349: GeomPoint X=42.0728 Y=-91.7794 Z=0
    g350: Circle CenterX=2.07281 CenterY=-91.7794 CenterZ=0 NormalX=0 NormalY=0 NormalZ=1 AngleXU=0 Radius=1
    g351: Circle CenterX=-1.92719 CenterY=-91.7794 CenterZ=0 NormalX=0 NormalY=0 NormalZ=1 AngleXU=0 Radius=1
    g352: Circle CenterX=1.57905 CenterY=-89.8542 CenterZ=0 NormalX=0 NormalY=0 NormalZ=1 AngleXU=0 Radius=1
    g353: BSplineCurve PolesCount=3 KnotsCount=2 Degree=2 IsPeriodic=0
    g354: GeomPoint X=2.07281 Y=-91.7794 Z=0
    g355: GeomPoint X=1.57905 Y=-89.8542 Z=0
  constraints (600):
    c: Coincident(g3,g2)
    c: Coincident(g0,g4)
    c: Block(g3)
    c: Block(g2)
    c: Block(g0)
    c: Block(g1)
    c: Vertical(g5)
    c: Vertical(g6)
    c: Block(g6)
    c: Block(g5)
    c: Tangent(g7,g10) = 1.5708
    c: Tangent(g7,g9) = -1.5708
    c: Tangent(g9,g8) = -1.5708
    c: Tangent(g10,g8) = 1.5708
    c: Vertical(g9)
    c: Equal(g7,g8)
    c: Block(g10)
    c: Block(g9)
    c: Tangent(g11,g12) = 1.5708
    c: Tangent(g12,g14) = 1.5708
    c: Equal(g11,g14)
    c: Coincident(g13,g11)
    c: Coincident(g13,g14)
    c: Block(g12)
    c: Block(g13)
    c: Weight(g15) = 1
    c: Equal(g15,g16)
    c: Equal(g15,g17)
    c: InternalAlignment(g15,g18)
    c: InternalAlignment(g16,g18)
    c: InternalAlignment(g17,g18)
    c: InternalAlignment(g19,g18)
    c: InternalAlignment(g20,g18)
    c: Weight(g21) = 1
    c: Equal(g21,g22)
    c: Equal(g21,g23)
    c: InternalAlignment(g21,g24)
    c: InternalAlignment(g22,g24)
    c: InternalAlignment(g23,g24)
    c: InternalAlignment(g25,g24)
    c: InternalAlignment(g26,g24)
    c: Block(g24)
    c: Block(g18)
    c: Weight(g27) = 1
    c: Equal(g27,g28)
    c: Equal(g27,g29)
    c: InternalAlignment(g27,g30)
    c: InternalAlignment(g28,g30)
    c: InternalAlignment(g29,g30)
    c: InternalAlignment(g31,g30)
    c: InternalAlignment(g32,g30)
    c: Weight(g33) = 1
    c: Equal(g33,g34)
    c: Equal(g33,g35)
    c: InternalAlignment(g33,g36)
    c: InternalAlignment(g34,g36)
    c: InternalAlignment(g35,g36)
    c: InternalAlignment(g37,g36)
    c: InternalAlignment(g38,g36)
    c: Block(g36)
    c: Block(g30)
    c: Weight(g39) = 1
    c: Equal(g39,g40)
    c: Equal(g39,g41)
    c: InternalAlignment(g39,g42)
    c: InternalAlignment(g40,g42)
    c: InternalAlignment(g41,g42)
    c: InternalAlignment(g43,g42)
    c: InternalAlignment(g44,g42)
    c: Weight(g45) = 1
    c: Equal(g45,g46)
    c: Equal(g45,g47)
    c: InternalAlignment(g45,g48)
    c: InternalAlignment(g46,g48)
    c: InternalAlignment(g47,g48)
    c: InternalAlignment(g49,g48)
    c: InternalAlignment(g50,g48)
    c: Block(g42)
    c: Block(g48)
    c: Coincident(g51,g6)
    c: Coincident(g51,g5)
    c: Horizontal(g51)
    c: Distance(g51) = 450
    c: Coincident(g52,g6)
    c: Coincident(g52,g5)
    c: Horizontal(g52)
    c: Horizontal(g53)
    c: Coincident(g4,g53)
    c: Block(g53)
    c: Coincident(g1,g53)
    c: Weight(g54) = 1
    c: Equal(g54,g55)
    c: Equal(g54,g56)
    c: InternalAlignment(g54,g57)
    c: InternalAlignment(g55,g57)
    c: InternalAlignment(g56,g57)
    c: InternalAlignment(g58,g57)
    c: InternalAlignment(g59,g57)
    c: Block(g57)
    c: Weight(g60) = 1
    c: Equal(g60,g61)
    c: Equal(g60,g62)
    c: InternalAlignment(g60,g63)
    c: InternalAlignment(g61,g63)
    c: InternalAlignment(g62,g63)
    c: InternalAlignment(g64,g63)
    c: InternalAlignment(g65,g63)
    c: Block(g63)
    c: Weight(g66) = 1
    c: Equal(g66,g67)
    c: Equal(g66,g68)
    c: InternalAlignment(g66,g69)
    c: InternalAlignment(g67,g69)
    c: InternalAlignment(g68,g69)
    c: InternalAlignment(g70,g69)
    c: InternalAlignment(g71,g69)
    c: Block(g69)
    c: Weight(g72) = 1
    c: Equal(g72,g73)
    c: Equal(g72,g74)
    c: InternalAlignment(g72,g75)
    c: InternalAlignment(g73,g75)
    c: InternalAlignment(g74,g75)
    c: InternalAlignment(g76,g75)
    c: InternalAlignment(g77,g75)
    c: Block(g75)
    c: Weight(g78) = 1
    c: Equal(g78,g79)
    c: Equal(g78,g80)
    c: InternalAlignment(g78,g81)
    c: InternalAlignment(g79,g81)
    c: InternalAlignment(g80,g81)
    c: InternalAlignment(g82,g81)
    c: InternalAlignment(g83,g81)
    c: Weight(g84) = 1
    c: Equal(g84,g85)
    c: Equal(g84,g86)
    c: InternalAlignment(g84,g87)
    c: InternalAlignment(g85,g87)
    c: InternalAlignment(g86,g87)
    c: InternalAlignment(g88,g87)
    c: InternalAlignment(g89,g87)
    c: Block(g81)
    c: Block(g87)
    c: Coincident(g90,g81)
    c: Coincident(g90,g87)
    c: Vertical(g90)
    c: Coincident(g91,g81)
    c: Coincident(g91,g63)
    c: Coincident(g92,g63)
    c: Coincident(g92,g87)
    c: Weight(g93) = 1
    c: Equal(g93,g94)
    c: Equal(g93,g95)
    c: InternalAlignment(g93,g96)
    c: InternalAlignment(g94,g96)
    c: InternalAlignment(g95,g96)
    c: InternalAlignment(g97,g96)
    c: InternalAlignment(g98,g96)
    c: Weight(g99) = 1
    c: Equal(g99,g100)
    c: Equal(g99,g101)
    c: InternalAlignment(g99,g102)
    c: InternalAlignment(g100,g102)
    c: InternalAlignment(g101,g102)
    c: InternalAlignment(g103,g102)
    c: InternalAlignment(g104,g102)
    c: Block(g96)
    c: Block(g102)
    c: Coincident(g105,g96)
    c: Coincident(g105,g102)
    c: Vertical(g105)
    c: Coincident(g106,g96)
    c: Coincident(g106,g57)
    c: Coincident(g107,g57)
    c: Coincident(g107,g102)
    c: Weight(g108) = 1
    c: Equal(g108,g109)
    c: Equal(g108,g110)
    c: InternalAlignment(g108,g111)
    c: InternalAlignment(g109,g111)
    c: InternalAlignment(g110,g111)
    c: InternalAlignment(g112,g111)
    c: InternalAlignment(g113,g111)
    c: Weight(g114) = 1
    c: Equal(g114,g115)
    c: Equal(g114,g116)
    c: InternalAlignment(g114,g117)
    c: InternalAlignment(g115,g117)
    c: InternalAlignment(g116,g117)
    c: InternalAlignment(g118,g117)
    c: InternalAlignment(g119,g117)
    c: Block(g111)
    c: Block(g117)
    c: Coincident(g120,g111)
    c: Coincident(g120,g117)
    c: Vertical(g120)
    c: Coincident(g121,g117)
    c: Coincident(g121,g75)
    c: Coincident(g122,g75)
    c: Coincident(g122,g111)
    c: Weight(g123) = 1
    c: Equal(g123,g124)
    c: Equal(g123,g125)
    c: InternalAlignment(g123,g126)
    c: InternalAlignment(g124,g126)
    c: InternalAlignment(g125,g126)
    c: InternalAlignment(g127,g126)
    c: InternalAlignment(g128,g126)
    c: Weight(g129) = 1
    c: Equal(g129,g130)
    c: Equal(g129,g131)
    c: InternalAlignment(g129,g132)
    c: InternalAlignment(g130,g132)
    c: InternalAlignment(g131,g132)
    c: InternalAlignment(g133,g132)
    c: InternalAlignment(g134,g132)
    c: Block(g126)
    c: Block(g132)
    c: Coincident(g135,g126)
    c: Coincident(g135,g132)
    c: Vertical(g135)
    c: Coincident(g136,g132)
    c: Coincident(g136,g69)
    c: Coincident(g137,g69)
    c: Coincident(g137,g126)
    c: Weight(g138) = 1
    c: Equal(g138,g139)
    c: Equal(g138,g140)
    c: InternalAlignment(g138,g141)
    c: InternalAlignment(g139,g141)
    c: InternalAlignment(g140,g141)
    c: InternalAlignment(g142,g141)
    c: InternalAlignment(g143,g141)
    c: Weight(g144) = 1
    c: Equal(g144,g145)
    c: Equal(g144,g146)
    c: InternalAlignment(g144,g147)
    c: InternalAlignment(g145,g147)
    c: InternalAlignment(g146,g147)
    c: InternalAlignment(g148,g147)
    c: InternalAlignment(g149,g147)
    c: Weight(g150) = 1
    c: Equal(g150,g151)
    c: Equal(g150,g152)
    c: InternalAlignment(g150,g153)
    c: InternalAlignment(g151,g153)
    c: InternalAlignment(g152,g153)
    c: InternalAlignment(g154,g153)
    c: InternalAlignment(g155,g153)
    c: Weight(g156) = 1
    c: Equal(g156,g157)
    c: Equal(g156,g158)
    c: InternalAlignment(g156,g159)
    c: InternalAlignment(g157,g159)
    c: InternalAlignment(g158,g159)
    c: InternalAlignment(g160,g159)
    c: InternalAlignment(g161,g159)
    c: Block(g159)
    c: Block(g153)
    c: Block(g147)
    c: Block(g141)
    c: Coincident(g162,g36)
    c: Coincident(g162,g159)
    c: Coincident(g163,g159)
    c: Coincident(g163,g153)
    c: Horizontal(g163)
    c: Coincident(g164,g153)
    c: Coincident(g164,g36)
    c: Vertical(g164)
    c: Coincident(g165,g30)
    c: Coincident(g165,g147)
    c: Vertical(g165)
    c: Coincident(g166,g147)
    c: Coincident(g166,g141)
    c: Horizontal(g166)
    c: Coincident(g167,g141)
    c: Coincident(g167,g30)
    c: Weight(g168) = 1
    c: Equal(g168,g169)
    c: Equal(g168,g170)
    c: InternalAlignment(g168,g171)
    c: InternalAlignment(g169,g171)
    c: InternalAlignment(g170,g171)
    c: InternalAlignment(g172,g171)
    c: InternalAlignment(g173,g171)
    c: Weight(g174) = 1
    c: Equal(g174,g175)
    c: Equal(g174,g176)
    c: InternalAlignment(g174,g177)
    c: InternalAlignment(g175,g177)
    c: InternalAlignment(g176,g177)
    c: InternalAlignment(g178,g177)
    c: InternalAlignment(g179,g177)
    c: Weight(g180) = 1
    c: Equal(g180,g181)
    c: Equal(g180,g182)
    c: InternalAlignment(g180,g183)
    c: InternalAlignment(g181,g183)
    c: InternalAlignment(g182,g183)
    c: InternalAlignment(g184,g183)
    c: InternalAlignment(g185,g183)
    c: Weight(g186) = 1
    c: Equal(g186,g187)
    c: Equal(g186,g188)
    c: InternalAlignment(g186,g189)
    c: InternalAlignment(g187,g189)
    c: InternalAlignment(g188,g189)
    c: InternalAlignment(g190,g189)
    c: InternalAlignment(g191,g189)
    c: Block(g189)
    c: Block(g183)
    c: Block(g177)
    c: Block(g171)
    c: Coincident(g192,g189)
    c: Coincident(g192,g183)
    c: Horizontal(g192)
    c: Coincident(g193,g183)
    c: Coincident(g193,g18)
    c: Vertical(g193)
    c: Coincident(g194,g24)
    c: Coincident(g194,g177)
    c: Vertical(g194)
    c: Coincident(g195,g177)
    c: Coincident(g195,g171)
    c: Horizontal(g195)
    c: Coincident(g196,g171)
    c: Coincident(g196,g24)
    c: Coincident(g197,g18)
    c: Weight(g198) = 1
    c: Equal(g198,g199)
    c: Equal(g198,g200)
    c: InternalAlignment(g198,g201)
    c: InternalAlignment(g199,g201)
    c: InternalAlignment(g200,g201)
    c: InternalAlignment(g202,g201)
    c: InternalAlignment(g203,g201)
    c: Weight(g204) = 1
    c: Equal(g204,g205)
    c: Equal(g204,g206)
    c: InternalAlignment(g204,g207)
    c: InternalAlignment(g205,g207)
    c: InternalAlignment(g206,g207)
    c: InternalAlignment(g208,g207)
    c: InternalAlignment(g209,g207)
    c: Block(g207)
    c: Block(g201)
    c: Coincident(g210,g207)
    c: Coincident(g210,g42)
    c: Coincident(g211,g42)
    c: Coincident(g211,g201)
    c: Coincident(g212,g201)
    c: Coincident(g212,g207)
    c: Vertical(g212)
    c: Weight(g213) = 1
    c: Equal(g213,g214)
    c: Equal(g213,g215)
    c: InternalAlignment(g213,g216)
    c: InternalAlignment(g214,g216)
    c: InternalAlignment(g215,g216)
    c: InternalAlignment(g217,g216)
    c: InternalAlignment(g218,g216)
    c: Weight(g219) = 1
    c: Equal(g219,g220)
    c: Equal(g219,g221)
    c: InternalAlignment(g219,g222)
    c: InternalAlignment(g220,g222)
    c: InternalAlignment(g221,g222)
    c: InternalAlignment(g223,g222)
    c: InternalAlignment(g224,g222)
    c: Block(g222)
    c: Block(g216)
    c: Coincident(g225,g216)
    c: Coincident(g225,g48)
    c: Coincident(g226,g48)
    c: Coincident(g226,g222)
    c: Coincident(g227,g222)
    c: Coincident(g227,g216)
    c: Vertical(g227)
    c: Horizontal(g228)
    c: Block(g228)
    c: Vertical(g229)
    c: Block(g229)
    c: Block(g230)
    c: Weight(g231) = 1
    c: Equal(g231,g232)
    c: Equal(g231,g233)
    c: InternalAlignment(g231,g234)
    c: InternalAlignment(g232,g234)
    c: InternalAlignment(g233,g234)
    c: InternalAlignment(g235,g234)
    c: InternalAlignment(g236,g234)
    c: Weight(g237) = 1
    c: Equal(g237,g238)
    c: Equal(g237,g239)
    c: InternalAlignment(g237,g240)
    c: InternalAlignment(g238,g240)
    c: InternalAlignment(g239,g240)
    c: InternalAlignment(g241,g240)
    c: InternalAlignment(g242,g240)
    c: Weight(g243) = 1
    c: Equal(g243,g244)
    c: Equal(g243,g245)
    c: InternalAlignment(g243,g246)
    c: InternalAlignment(g244,g246)
    c: InternalAlignment(g245,g246)
    c: InternalAlignment(g247,g246)
    c: InternalAlignment(g248,g246)
    c: Weight(g249) = 1
    c: Equal(g249,g250)
    c: Equal(g249,g251)
    c: InternalAlignment(g249,g252)
    c: InternalAlignment(g250,g252)
    c: InternalAlignment(g251,g252)
    c: InternalAlignment(g253,g252)
    c: InternalAlignment(g254,g252)
    c: Block(g234)
    c: Block(g240)
    c: Block(g246)
    c: Block(g252)
    c: Coincident(g255,g240)
    c: Coincident(g255,g234)
    c: Horizontal(g255)
    c: Block(g197)
    c: Weight(g256) = 1
    c: Equal(g256,g257)
    c: Equal(g256,g258)
    c: InternalAlignment(g256,g259)
    c: InternalAlignment(g257,g259)
    c: InternalAlignment(g258,g259)
    c: InternalAlignment(g260,g259)
    c: InternalAlignment(g261,g259)
    c: Weight(g262) = 1
    c: Equal(g262,g263)
    c: Equal(g262,g264)
    c: InternalAlignment(g262,g265)
    c: InternalAlignment(g263,g265)
    c: InternalAlignment(g264,g265)
    c: InternalAlignment(g266,g265)
    c: InternalAlignment(g267,g265)
    c: Weight(g268) = 1
    c: Equal(g268,g269)
    c: Equal(g268,g270)
    c: InternalAlignment(g268,g271)
    c: InternalAlignment(g269,g271)
    c: InternalAlignment(g270,g271)
    c: InternalAlignment(g272,g271)
    c: InternalAlignment(g273,g271)
    c: Weight(g274) = 1
    c: Equal(g274,g275)
    c: Equal(g274,g276)
    c: InternalAlignment(g274,g277)
    c: InternalAlignment(g275,g277)
    c: InternalAlignment(g276,g277)
    c: InternalAlignment(g278,g277)
    c: InternalAlignment(g279,g277)
    c: Block(g259)
    c: Block(g265)
    c: Block(g271)
    c: Block(g277)
    c: Coincident(g280,g271)
    c: Coincident(g280,g277)
    c: Horizontal(g280)
    c: Coincident(g281,g277)
    c: Coincident(g281,g259)
    c: Vertical(g281)
    c: Coincident(g282,g259)
    c: Coincident(g282,g265)
    c: Coincident(g283,g265)
    c: Coincident(g283,g271)
    c: Vertical(g283)
    c: Weight(g284) = 1
    c: Equal(g284,g285)
    c: Equal(g284,g286)
    c: InternalAlignment(g284,g287)
    c: InternalAlignment(g285,g287)
    c: InternalAlignment(g286,g287)
    c: InternalAlignment(g288,g287)
    c: InternalAlignment(g289,g287)
    c: Weight(g290) = 1
    c: Equal(g290,g291)
    c: Equal(g290,g292)
    c: InternalAlignment(g290,g293)
    c: InternalAlignment(g291,g293)
    c: InternalAlignment(g292,g293)
    c: InternalAlignment(g294,g293)
    c: InternalAlignment(g295,g293)
    c: Weight(g296) = 1
    c: Equal(g296,g297)
    c: Equal(g296,g298)
    c: InternalAlignment(g296,g299)
    c: InternalAlignment(g297,g299)
    c: InternalAlignment(g298,g299)
    c: InternalAlignment(g300,g299)
    c: InternalAlignment(g301,g299)
    c: Block(g299)
    c: Block(g293)
    c: Block(g287)
    c: Coincident(g302,g293)
    c: Coincident(g302,g287)
    c: Coincident(g303,g287)
    c: Coincident(g303,g299)
    c: Vertical(g303)
    c: Coincident(g304,g299)
    c: Coincident(g304,g293)
    c: Horizontal(g304)
    c: Weight(g305) = 1
    c: Equal(g305,g306)
    c: InternalAlignment(g305,g307)
    c: InternalAlignment(g306,g307)
    c: InternalAlignment(g308,g307)
    c: InternalAlignment(g309,g307)
    c: Weight(g310) = 1
    c: Equal(g310,g311)
    c: Equal(g310,g312)
    c: InternalAlignment(g310,g313)
    c: InternalAlignment(g311,g313)
    c: InternalAlignment(g312,g313)
    c: InternalAlignment(g314,g313)
    c: InternalAlignment(g315,g313)
    c: Weight(g316) = 1
    c: Equal(g316,g317)
    c: Equal(g316,g318)
    c: InternalAlignment(g316,g319)
    c: InternalAlignment(g317,g319)
    c: InternalAlignment(g318,g319)
    c: InternalAlignment(g320,g319)
    c: InternalAlignment(g321,g319)
    c: Equal(g322,g323)
    c: Equal(g322,g324)
    c: InternalAlignment(g322,g325)
    c: InternalAlignment(g323,g325)
    c: InternalAlignment(g324,g325)
    c: InternalAlignment(g326,g325)
    c: InternalAlignment(g327,g325)
    c: Block(g313)
    c: Block(g319)
    c: Block(g325)
    c: Block(g307)
    c: Coincident(g328,g307)
    c: Coincident(g328,g313)
    c: Horizontal(g328)
    c: Coincident(g329,g313)
    c: Coincident(g329,g319)
    c: Vertical(g329)
    c: Coincident(g330,g319)
    c: Coincident(g330,g325)
    c: Horizontal(g330)
    c: Coincident(g331,g325)
    c: Coincident(g331,g307)
    c: Vertical(g332)
    c: Vertical(g333)
    c: Horizontal(g334)
    c: Horizontal(g335)
    c: Distance(g335) = 4
    c: Distance(g334) = 4
    c: Distance(g336) = 4
    c: Distance(g337) = 4
    c: Distance(g332) = 4
    c: Distance(g333) = 4
    c: Parallel(g2,g337)
    c: Parallel(g336,g2)
    c: Coincident(g333,g3)
    c: Coincident(g334,g3)
    c: Coincident(g335,g2)
    c: Coincident(g332,g2)
    c: Coincident(g337,g2)
    c: Coincident(g341,g337)
    c: Weight(g338) = 1
    c: Equal(g338,g339)
    c: Coincident(g339,g2)
    c: Equal(g338,g340)
    c: Coincident(g341,g332)
    c: InternalAlignment(g338,g341)
    c: InternalAlignment(g339,g341)
    c: InternalAlignment(g340,g341)
    c: InternalAlignment(g342,g341)
    c: InternalAlignment(g343,g341)
    c: Coincident(g347,g333)
    c: Weight(g344) = 1
    c: Equal(g344,g345)
    c: Coincident(g345,g3)
    c: Equal(g344,g346)
    c: Coincident(g347,g334)
    c: InternalAlignment(g344,g347)
    c: InternalAlignment(g345,g347)
    c: InternalAlignment(g346,g347)
    c: InternalAlignment(g348,g347)
    c: InternalAlignment(g349,g347)
    c: Coincident(g353,g335)
    c: Weight(g350) = 1
    c: Equal(g350,g351)
    c: Coincident(g351,g2)
    c: Equal(g350,g352)
    c: Coincident(g353,g336)
    c: InternalAlignment(g350,g353)
    c: InternalAlignment(g351,g353)
    c: InternalAlignment(g352,g353)
    c: InternalAlignment(g354,g353)
    c: InternalAlignment(g355,g353)
FEATURE [Sketcher::SketchObject] Sketch001
  FullyConstrained = true
  MapMode = 4
  Placement = pos=(0,0,0) rot=(0.57735,0.57735,0.57735;2.0944rad)
  Support = -> [Sketch]
  sketch-geometry (46):
    g0: BSplineCurve PolesCount=3 KnotsCount=2 Degree=2 IsPeriodic=0
    g1: ArcOfCircle CenterX=73.1223 CenterY=-32.291 CenterZ=0 NormalX=0 NormalY=0 NormalZ=1 AngleXU=0 Radius=13 StartAngle=5.92268 EndAngle=9.06428
    g2: ArcOfCircle CenterX=66.7816 CenterY=-49.1439 CenterZ=0 NormalX=0 NormalY=0 NormalZ=1 AngleXU=0 Radius=13 StartAngle=2.78068 EndAngle=5.92131
    g3: ArcOfCircle CenterX=55.9263 CenterY=-78.1807 CenterZ=0 NormalX=0 NormalY=0 NormalZ=1 AngleXU=0 Radius=13 StartAngle=5.92268 EndAngle=9.06428
    g4: ArcOfCircle CenterX=49.5884 CenterY=-95.0342 CenterZ=0 NormalX=0 NormalY=0 NormalZ=1 AngleXU=0 Radius=13 StartAngle=2.78068 EndAngle=5.92131
    g5: ArcOfCircle CenterX=38.7206 CenterY=-124.067 CenterZ=0 NormalX=0 NormalY=0 NormalZ=1 AngleXU=0 Radius=13 StartAngle=5.92268 EndAngle=9.06428
    g6: ArcOfCircle CenterX=32.3875 CenterY=-140.92 CenterZ=0 NormalX=0 NormalY=0 NormalZ=1 AngleXU=0 Radius=13 StartAngle=2.78068 EndAngle=5.92131
    g7: ArcOfCircle CenterX=21.4715 CenterY=-169.934 CenterZ=0 NormalX=0 NormalY=0 NormalZ=1 AngleXU=0 Radius=13 StartAngle=5.92268 EndAngle=9.06428
    g8: ArcOfCircle CenterX=15.1336 CenterY=-186.787 CenterZ=0 NormalX=0 NormalY=0 NormalZ=1 AngleXU=0 Radius=13 StartAngle=2.78068 EndAngle=5.92131
    g9-g12: Circle x4 (B-spline internal-alignment scaffolding for g13; pole/knot coordinates omitted)
    g13: BSplineCurve PolesCount=4 KnotsCount=2 Degree=3 IsPeriodic=0
    g14: GeomPoint X=28.8094 Y=-19.0875 Z=0
    g15: GeomPoint X=47.0443 Y=-50.4712 Z=0
    g16: Circle CenterX=53.5586 CenterY=-23.2695 CenterZ=0 NormalX=0 NormalY=0 NormalZ=1 AngleXU=0 Radius=3.24518
    g17: Circle CenterX=-195.441 CenterY=-127.082 CenterZ=0 NormalX=0 NormalY=0 NormalZ=1 AngleXU=0 Radius=1
    g18: Circle CenterX=-8.24091 CenterY=-197.481 CenterZ=0 NormalX=0 NormalY=0 NormalZ=1 AngleXU=0 Radius=1
    g19: Circle CenterX=12.8789 CenterY=-141.321 CenterZ=0 NormalX=0 NormalY=0 NormalZ=1 AngleXU=0 Radius=1
    g20: BSplineCurve PolesCount=3 KnotsCount=2 Degree=2 IsPeriodic=0
    g21: GeomPoint X=-195.441 Y=-127.082 Z=0
    g22: GeomPoint X=12.8789 Y=-141.321 Z=0
    g23: Circle CenterX=-12.8016 CenterY=-179.036 CenterZ=0 NormalX=0 NormalY=0 NormalZ=1 AngleXU=0 Radius=10.5072
    g24: Circle CenterX=0.933922 CenterY=-166.43 CenterZ=0 NormalX=0 NormalY=0 NormalZ=1 AngleXU=0 Radius=3.26661
    g25: Circle CenterX=-33.5518 CenterY=-176.44 CenterZ=0 NormalX=0 NormalY=0 NormalZ=1 AngleXU=0 Radius=5.64388
    g26: Circle CenterX=-47.2366 CenterY=-173.859 CenterZ=0 NormalX=0 NormalY=0 NormalZ=1 AngleXU=0 Radius=3.01653
    g27: Circle CenterX=-56.2595 CenterY=-171.456 CenterZ=0 NormalX=0 NormalY=0 NormalZ=1 AngleXU=0 Radius=2.12826
    g28: ArcOfCircle CenterX=51.2151 CenterY=-198.473 CenterZ=0 NormalX=0 NormalY=0 NormalZ=1 AngleXU=0 Radius=20 StartAngle=2.78189 EndAngle=4.35269
    g29: LineSegment StartX=32.4951 StartY=-191.433 StartZ=0 EndX=94.6578 EndY=-26.1352 EndZ=0
    g30: LineSegment StartX=43.1192 StartY=-220.001 StartZ=0 EndX=-196.497 EndY=-129.89 EndZ=0
    g31: LineSegment StartX=43.1192 StartY=-220.001 StartZ=0 EndX=44.1752 EndY=-217.193 EndZ=0
    g32: LineSegment StartX=117.223 StartY=-19.0875 StartZ=0 EndX=117.223 EndY=-16.0875 EndZ=0
    g33: LineSegment StartX=117.223 StartY=-16.0875 StartZ=0 EndX=17.2232 EndY=-16.0875 EndZ=0
    g34: LineSegment StartX=17.2232 StartY=-16.0875 StartZ=0 EndX=17.2232 EndY=-19.0875 EndZ=0
    g35: LineSegment StartX=28.8094 StartY=-19.0875 StartZ=0 EndX=17.2232 EndY=-19.0875 EndZ=0
    g36: LineSegment StartX=47.0443 StartY=-50.4712 StartZ=0 EndX=12.8789 EndY=-141.321 EndZ=0
    g37: LineSegment StartX=-195.441 StartY=-127.082 StartZ=0 EndX=-196.497 EndY=-129.89 EndZ=0
    g38: LineSegment StartX=85.2866 StartY=-36.8766 StartZ=0 EndX=78.9396 EndY=-53.7463 EndZ=0
    g39: LineSegment StartX=60.9579 StartY=-27.7053 StartZ=0 EndX=54.6191 EndY=-44.5532 EndZ=0
    g40: LineSegment StartX=68.0907 StartY=-82.7664 StartZ=0 EndX=61.7465 EndY=-99.6365 EndZ=0
    g41: LineSegment StartX=43.7619 StartY=-73.595 StartZ=0 EndX=37.426 EndY=-90.4435 EndZ=0
    g42: LineSegment StartX=50.885 StartY=-128.652 StartZ=0 EndX=44.5456 EndY=-145.522 EndZ=0
    g43: LineSegment StartX=26.5562 StartY=-119.481 StartZ=0 EndX=20.2251 EndY=-136.329 EndZ=0
    g44: LineSegment StartX=9.3071 StartY=-165.349 StartZ=0 EndX=2.97115 EndY=-182.197 EndZ=0
    g45: LineSegment StartX=33.6358 StartY=-174.52 StartZ=0 EndX=27.2917 EndY=-191.39 EndZ=0
  constraints (71):
    c: Block(g0)
    c: Block(g1)
    c: Block(g2)
    c: Block(g4)
    c: Block(g3)
    c: Block(g6)
    c: Block(g5)
    c: Block(g8)
    c: Block(g7)
    c: Weight(g9) = 1
    c: Equal(g9,g10)
    c: Equal(g9,g11)
    c: Equal(g9,g12)
    c: InternalAlignment(g9-g12 -> g13) x4
    c: InternalAlignment(g14,g13)
    c: InternalAlignment(g15,g13)
    c: Block(g16)
    c: Weight(g17) = 1
    c: Equal(g17,g18)
    c: Equal(g17,g19)
    c: InternalAlignment(g17,g20)
    c: InternalAlignment(g18,g20)
    c: InternalAlignment(g19,g20)
    c: InternalAlignment(g21,g20)
    c: InternalAlignment(g22,g20)
    c: Block(g20)
    c: Block(g23)
    c: Block(g24)
    c: Block(g25)
    c: Block(g26)
    c: Block(g27)
    c: Block(g28)
    c: Coincident(g29,g28)
    c: Coincident(g29,g0)
    c: Block(g13)
    c: Coincident(g31,g30)
    c: Coincident(g31,g28)
    c: Block(g31)
    c: Coincident(g32,g0)
    c: Vertical(g32)
    c: Coincident(g33,g32)
    c: Horizontal(g33)
    c: Coincident(g34,g33)
    c: Vertical(g34)
    c: Block(g33)
    c: Coincident(g35,g13)
    c: Coincident(g35,g34)
    c: Horizontal(g35)
    c: Coincident(g36,g13)
    c: Coincident(g36,g20)
    c: Coincident(g37,g20)
    c: Coincident(g37,g30)
    c: Block(g30)
    c: Coincident(g38,g1)
    c: Coincident(g38,g2)
    c: Coincident(g39,g1)
    c: Coincident(g39,g2)
    c: Coincident(g40,g3)
    c: Coincident(g40,g4)
    c: Coincident(g41,g3)
    c: Coincident(g41,g4)
    c: Coincident(g42,g5)
    c: Coincident(g42,g6)
    c: Coincident(g43,g5)
    c: Coincident(g43,g6)
    c: Coincident(g44,g7)
    c: Coincident(g44,g8)
    c: Coincident(g45,g7)
    c: Coincident(g45,g8)
    c: Distance(g30) = 256
    c: Distance(g33) = 100
FEATURE [Part::Extrusion] Extrude002
  Base = -> Sketch001
  Dir = (1,0,0)
  DirMode = 2
  FaceMakerClass = Part::FaceMakerBullseye
  LengthFwd = 8
  LengthRev = 0
  Solid = true
  Symmetric = false
FEATURE [Sketcher::SketchObject] Sketch002
  FullyConstrained = true
  sketch-geometry (20):
    g0: LineSegment StartX=-2.77179 StartY=-200.304 StartZ=0 EndX=5.22821 EndY=-200.304 EndZ=0
    g1: LineSegment StartX=5.22821 StartY=-200.304 StartZ=0 EndX=5.22821 EndY=-197.304 EndZ=0
    g2: LineSegment StartX=-2.77179 StartY=-200.304 StartZ=0 EndX=-2.77179 EndY=-197.304 EndZ=0
    g3: LineSegment StartX=5.22821 StartY=-197.304 StartZ=0 EndX=8.22821 EndY=-197.304 EndZ=0
    g4: LineSegment StartX=-2.77179 StartY=-197.304 StartZ=0 EndX=-5.77179 EndY=-197.304 EndZ=0
    g5: LineSegment StartX=19.2282 StartY=-203.304 StartZ=0 EndX=19.2282 EndY=-206.304 EndZ=0
    g6: LineSegment StartX=-16.7718 StartY=-203.304 StartZ=0 EndX=-16.7718 EndY=-206.304 EndZ=0
    g7: LineSegment StartX=-16.7718 StartY=-206.304 StartZ=0 EndX=19.2282 EndY=-206.304 EndZ=0
    g8: Circle CenterX=-16.7718 CenterY=-203.304 CenterZ=0 NormalX=0 NormalY=0 NormalZ=1 AngleXU=0 Radius=1
    g9: Circle CenterX=-5.77179 CenterY=-203.304 CenterZ=0 NormalX=0 NormalY=0 NormalZ=1 AngleXU=0 Radius=1
    g10: Circle CenterX=-5.77179 CenterY=-197.304 CenterZ=0 NormalX=0 NormalY=0 NormalZ=1 AngleXU=0 Radius=1
    g11: BSplineCurve PolesCount=3 KnotsCount=2 Degree=2 IsPeriodic=0
    g12: GeomPoint X=-16.7718 Y=-203.304 Z=0
    g13: GeomPoint X=-5.77179 Y=-197.304 Z=0
    g14: Circle CenterX=19.2282 CenterY=-203.304 CenterZ=0 NormalX=0 NormalY=0 NormalZ=1 AngleXU=0 Radius=1
    g15: Circle CenterX=8.22821 CenterY=-203.304 CenterZ=0 NormalX=0 NormalY=0 NormalZ=1 AngleXU=0 Radius=1
    g16: Circle CenterX=8.22821 CenterY=-197.304 CenterZ=0 NormalX=0 NormalY=0 NormalZ=1 AngleXU=0 Radius=1
    g17: BSplineCurve PolesCount=3 KnotsCount=2 Degree=2 IsPeriodic=0
    g18: GeomPoint X=19.2282 Y=-203.304 Z=0
    g19: GeomPoint X=8.22821 Y=-197.304 Z=0
  constraints (41):
    c: Horizontal(g0)
    c: Distance(g0) = 8
    c: Coincident(g1,g0)
    c: Vertical(g1)
    c: Distance(g1) = 3
    c: Coincident(g2,g0)
    c: Vertical(g2)
    c: Distance(g2) = 3
    c: Coincident(g3,g1)
    c: Horizontal(g3)
    c: Distance(g3) = 3
    c: Coincident(g4,g2)
    c: Horizontal(g4)
    c: Distance(g4) = 3
    c: Vertical(g5)
    c: Vertical(g6)
    c: Coincident(g7,g6)
    c: Coincident(g7,g5)
    c: Weight(g8) = 1
    c: Equal(g8,g9)
    c: Equal(g8,g10)
    c: Coincident(g11,g4)
    c: InternalAlignment(g8,g11)
    c: InternalAlignment(g9,g11)
    c: InternalAlignment(g10,g11)
    c: InternalAlignment(g12,g11)
    c: InternalAlignment(g13,g11)
    c: Coincident(g17,g5)
    c: Weight(g14) = 1
    c: Equal(g14,g15)
    c: Equal(g14,g16)
    c: Coincident(g17,g3)
    c: InternalAlignment(g14,g17)
    c: InternalAlignment(g15,g17)
    c: InternalAlignment(g16,g17)
    c: InternalAlignment(g18,g17)
    c: InternalAlignment(g19,g17)
    c: Block(g7)
    c: Block(g17)
    c: Block(g11)
    c: Block(g6)
FEATURE [Part::Extrusion] Extrude003
  Base = -> Sketch002
  Dir = (0,0,1)
  DirMode = 2
  FaceMakerClass = Part::FaceMakerBullseye
  LengthFwd = 260
  LengthRev = 0
  Solid = true
  Symmetric = false
FEATURE [Part::Extrusion] Extrude
  Base = -> Sketch
  Dir = (0,0,1)
  DirMode = 2
  FaceMakerClass = Part::FaceMakerBullseye
  LengthFwd = 14
  LengthRev = 0
  Solid = true
  Symmetric = false
